# Revit family: 07. Wichmann Kabelbox W120
name_source: partatom
category: HLS-Bauteile
revit_build: Autodesk Revit 2018 (Build: 20170223_1515(x64)
units: mm (PartAtom-declared; Revit-internal decimal feet)

## family parameters
Basisbauteil = Wand
Beim Laden mit Abzugskörper schneiden = Nein
Bemaßung runder Anschluss = Durchmesser verwenden
Gemeinsam genutzt = Nein
Immer vertikal = Ja
Raumberechnungspunkt = Nein
Teiletyp = Normal

## types (68) — shared parameters
Rohbauöffnung = Ja
Tbox = 350 mm  [stored 1.14829 ft]

## per-type parameters (varying)
| type | BA | BI | BR | HA | HAN | HI | HR |
| Kabelbox W120, 90x200x350 mm | 640 mm | 610 mm | 680 mm | 100 mm  [stored 0.328084 ft] | W120090200 | 64 mm | 140 mm |
| Kabelbox W120, 90x180x350 mm | 180 mm | 150 mm  [stored 0.492126 ft] | 220 mm | 90 mm | W120090180 | 56 mm | 130 mm |
| Kabelbox W120, 90x160x350 mm | 160 mm | 130 mm | 200 mm  [stored 0.656168 ft] | 90 mm | W120090160 | 56 mm | 130 mm |
| Kabelbox W120, 90x120x350 mm | 120 mm  [stored 0.393701 ft] | 90 mm | 160 mm | 90 mm | W120090120 | 56 mm | 130 mm |
| Kabelbox W120, 90x90x350 mm | 90 mm | 60 mm | 130 mm | 90 mm | W120090090 | 56 mm | 130 mm |
| Kabelbox W120, 80x580x350 mm | 580 mm | 550 mm | 620 mm | 80 mm  [stored 0.262467 ft] | 00090090 | 50 mm  [stored 0.164042 ft] | 120 mm  [stored 0.393701 ft] |
| Kabelbox W120, 80x535x350 mm | 535 mm | 505 mm | 575 mm | 80 mm  [stored 0.262467 ft] | W120080535 | 50 mm  [stored 0.164042 ft] | 120 mm  [stored 0.393701 ft] |
| Kabelbox W120, 80x480x350 mm | 480 mm | 450 mm | 520 mm | 80 mm  [stored 0.262467 ft] | W120080480 | 50 mm  [stored 0.164042 ft] | 120 mm  [stored 0.393701 ft] |
| Kabelbox W120, 80x435x350 mm | 435 mm | 405 mm | 475 mm | 80 mm  [stored 0.262467 ft] | W120080435 | 50 mm  [stored 0.164042 ft] | 120 mm  [stored 0.393701 ft] |
| Kabelbox W120, 80x380x350 mm | 380 mm | 350 mm  [stored 1.14829 ft] | 420 mm | 80 mm  [stored 0.262467 ft] | W120080380 | 50 mm  [stored 0.164042 ft] | 120 mm  [stored 0.393701 ft] |
| Kabelbox W120, 80x335x350 mm | 335 mm | 305 mm | 375 mm | 80 mm  [stored 0.262467 ft] | W120080335 | 50 mm  [stored 0.164042 ft] | 120 mm  [stored 0.393701 ft] |
| Kabelbox W120, 80x280x350 mm | 280 mm  [stored 0.918635 ft] | 250 mm | 320 mm  [stored 1.04987 ft] | 80 mm  [stored 0.262467 ft] | W120080280 | 50 mm  [stored 0.164042 ft] | 120 mm  [stored 0.393701 ft] |
| Kabelbox W120, 80x240x350 mm | 240 mm | 210 mm | 280 mm  [stored 0.918635 ft] | 80 mm  [stored 0.262467 ft] | W120080240 | 50 mm  [stored 0.164042 ft] | 120 mm  [stored 0.393701 ft] |
| Kabelbox W120, 80x200x350 mm | 200 mm  [stored 0.656168 ft] | 170 mm | 240 mm | 80 mm  [stored 0.262467 ft] | W120080200 | 50 mm  [stored 0.164042 ft] | 120 mm  [stored 0.393701 ft] |
| Kabelbox W120, 80x180x350 mm | 180 mm | 150 mm  [stored 0.492126 ft] | 220 mm | 80 mm  [stored 0.262467 ft] | W120080180 | 50 mm  [stored 0.164042 ft] | 120 mm  [stored 0.393701 ft] |
| Kabelbox W120, 80x160x350 mm | 160 mm | 130 mm | 200 mm  [stored 0.656168 ft] | 80 mm  [stored 0.262467 ft] | W120080160 | 50 mm  [stored 0.164042 ft] | 120 mm  [stored 0.393701 ft] |
| Kabelbox W120, 80x120x350 mm | 120 mm  [stored 0.393701 ft] | 90 mm | 160 mm | 80 mm  [stored 0.262467 ft] | W120080120 | 50 mm  [stored 0.164042 ft] | 120 mm  [stored 0.393701 ft] |
| Kabelbox W120, 90x535x350 mm | 535 mm | 505 mm | 575 mm | 90 mm | W120090535 | 56 mm | 130 mm |
| Kabelbox W120, 90x480x350 mm | 480 mm | 450 mm | 520 mm | 90 mm | W120090480 | 56 mm | 130 mm |
| Kabelbox W120, 90x435x350 mm | 435 mm | 405 mm | 475 mm | 90 mm | W120090435 | 56 mm | 130 mm |
| Kabelbox W120, 90x380x350 mm | 380 mm | 350 mm  [stored 1.14829 ft] | 420 mm | 90 mm | W120090380 | 56 mm | 130 mm |
| Kabelbox W120, 90x335x350 mm | 335 mm | 305 mm | 375 mm | 90 mm | W120090335 | 56 mm | 130 mm |
| Kabelbox W120, 90x280x350 mm | 280 mm  [stored 0.918635 ft] | 250 mm | 320 mm  [stored 1.04987 ft] | 90 mm | W120090280 | 56 mm | 130 mm |
| Kabelbox W120, 90x240x350 mm | 240 mm | 210 mm | 280 mm  [stored 0.918635 ft] | 90 mm | W120090240 | 56 mm | 130 mm |
| Kabelbox W120, 80x640x350 mm | 640 mm | 610 mm | 680 mm | 80 mm  [stored 0.262467 ft] | W120080640 | 50 mm  [stored 0.164042 ft] | 120 mm  [stored 0.393701 ft] |
| Kabelbox W120, 60x580x350 mm | 580 mm | 550 mm | 620 mm | 60 mm | W120060580 | 33 mm | 100 mm  [stored 0.328084 ft] |
| Kabelbox W120, 60x640x350 mm | 640 mm | 610 mm | 680 mm | 60 mm | W120060640 | 33 mm | 100 mm  [stored 0.328084 ft] |
| Kabelbox W120, 80x90x350 mm | 90 mm | 60 mm | 130 mm | 80 mm  [stored 0.262467 ft] | W120080090 | 50 mm  [stored 0.164042 ft] | 120 mm  [stored 0.393701 ft] |
| Kabelbox W120, 90x580x350 mm | 580 mm | 550 mm | 620 mm | 90 mm | W120090580 | 56 mm | 130 mm |
| Kabelbox W120, 100x120x350 mm | 120 mm  [stored 0.393701 ft] | 90 mm | 160 mm | 100 mm  [stored 0.328084 ft] | W120100120 | 64 mm | 140 mm |
| Kabelbox W120, 100x160x350 mm | 160 mm | 130 mm | 200 mm  [stored 0.656168 ft] | 100 mm  [stored 0.328084 ft] | W120100160 | 64 mm | 140 mm |
| Kabelbox W120, 100x180x350 mm | 180 mm | 150 mm  [stored 0.492126 ft] | 220 mm | 100 mm  [stored 0.328084 ft] | W120100180 | 64 mm | 140 mm |
| Kabelbox W120, 100x380x350 mm | 380 mm | 350 mm  [stored 1.14829 ft] | 420 mm | 100 mm  [stored 0.328084 ft] | W120100380 | 64 mm | 140 mm |
| Kabelbox W120, 90x640x350 mm | 640 mm | 610 mm | 680 mm | 90 mm | W120090640 | 56 mm | 130 mm |
| Kabelbox W120, 100x240x350 mm | 240 mm | 210 mm | 280 mm  [stored 0.918635 ft] | 100 mm  [stored 0.328084 ft] | W120100240 | 64 mm | 140 mm |
| Kabelbox W120, 100x200x350 mm | 200 mm  [stored 0.656168 ft] | 170 mm | 240 mm | 100 mm  [stored 0.328084 ft] | W120100200 | 64 mm | 140 mm |
| Kabelbox W120, 100x435x350 mm | 435 mm | 405 mm | 475 mm | 100 mm  [stored 0.328084 ft] | W120100435 | 64 mm | 140 mm |
| Kabelbox W120, 100x335x350 mm | 335 mm | 305 mm | 375 mm | 100 mm  [stored 0.328084 ft] | W120100335
W120100335
W120100335 | 64 mm | 140 mm |
| Kabelbox W120, 100x280x350 mm | 280 mm  [stored 0.918635 ft] | 250 mm | 320 mm  [stored 1.04987 ft] | 100 mm  [stored 0.328084 ft] | W120100280 | 64 mm | 140 mm |
| Kabelbox W120, 100x580x350 mm | 580 mm | 550 mm | 620 mm | 100 mm  [stored 0.328084 ft] | W120100580 | 64 mm | 140 mm |
| Kabelbox W120, 100x640x350 mm | 640 mm | 610 mm | 680 mm | 100 mm  [stored 0.328084 ft] | W120100640 | 64 mm | 140 mm |
| Kabelbox W120, 110x120x350 mm | 120 mm  [stored 0.393701 ft] | 90 mm | 160 mm | 110 mm | W120110120 | 70 mm | 150 mm  [stored 0.492126 ft] |
| Kabelbox W120, 100x480x350 mm | 480 mm | 450 mm | 520 mm | 100 mm  [stored 0.328084 ft] | W120100480 | 64 mm | 140 mm |
| Kabelbox W120, 100x535x350 mm | 535 mm | 505 mm | 575 mm | 100 mm  [stored 0.328084 ft] | W120100535 | 64 mm | 140 mm |
| Kabelbox W120, 110x180x350 mm | 180 mm | 150 mm  [stored 0.492126 ft] | 220 mm | 110 mm | W120110180 | 70 mm | 150 mm  [stored 0.492126 ft] |
| Kabelbox W120, 110x160x350 mm | 160 mm | 130 mm | 200 mm  [stored 0.656168 ft] | 110 mm | W120110160 | 70 mm | 150 mm  [stored 0.492126 ft] |
| Kabelbox W120, 110x280x350 mm | 280 mm  [stored 0.918635 ft] | 250 mm | 320 mm  [stored 1.04987 ft] | 110 mm | W120110280 | 70 mm | 150 mm  [stored 0.492126 ft] |
| Kabelbox W120, 110x240x350 mm | 240 mm | 210 mm | 280 mm  [stored 0.918635 ft] | 110 mm | W120110240 | 70 mm | 150 mm  [stored 0.492126 ft] |
| Kabelbox W120, 110x200x350 mm | 200 mm  [stored 0.656168 ft] | 170 mm | 240 mm | 110 mm | W120110200 | 70 mm | 150 mm  [stored 0.492126 ft] |
| Kabelbox W120, 110x435x350 mm | 435 mm | 405 mm | 475 mm | 110 mm | W120110435 | 70 mm | 150 mm  [stored 0.492126 ft] |
| Kabelbox W120, 110x480x350 mm | 480 mm | 450 mm | 520 mm | 110 mm | W120110480 | 70 mm | 150 mm  [stored 0.492126 ft] |
| Kabelbox W120, 110x535x350 mm | 535 mm | 505 mm | 575 mm | 110 mm | W120110535 | 70 mm | 150 mm  [stored 0.492126 ft] |
| Kabelbox W120, 110x335x350 mm | 335 mm | 305 mm | 375 mm | 110 mm | W120110535 | 70 mm | 150 mm  [stored 0.492126 ft] |
| Kabelbox W120, 110x380x350 mm | 380 mm | 350 mm  [stored 1.14829 ft] | 420 mm | 110 mm | W120110380 | 70 mm | 150 mm  [stored 0.492126 ft] |
| Kabelbox W120, 110x640x350 mm | 640 mm | 610 mm | 680 mm | 110 mm | W120110640 | 70 mm | 150 mm  [stored 0.492126 ft] |
| Kabelbox W120, 110x580x350 mm | 580 mm | 550 mm | 620 mm | 110 mm | W120110580 | 70 mm | 150 mm  [stored 0.492126 ft] |
| Kabelbox W120, 60x160x350 mm | 160 mm | 130 mm | 200 mm  [stored 0.656168 ft] | 60 mm | W120060160 | 33 mm | 100 mm  [stored 0.328084 ft] |
| Kabelbox W120, 60x120x350 mm | 120 mm  [stored 0.393701 ft] | 90 mm | 160 mm | 60 mm | W120060120 | 33 mm | 100 mm  [stored 0.328084 ft] |
| Kabelbox W120, 60x90x350 mm | 90 mm | 60 mm | 130 mm | 60 mm | W120060090 | 33 mm | 100 mm  [stored 0.328084 ft] |
| Kabelbox W120, 60x240x350 mm | 240 mm | 210 mm | 280 mm  [stored 0.918635 ft] | 60 mm | W120060240 | 33 mm | 100 mm  [stored 0.328084 ft] |
| Kabelbox W120, 60x280x350 mm | 280 mm  [stored 0.918635 ft] | 250 mm | 320 mm  [stored 1.04987 ft] | 60 mm | W120060280 | 33 mm | 100 mm  [stored 0.328084 ft] |
| Kabelbox W120, 60x335x350 mm | 335 mm | 305 mm | 375 mm | 60 mm | W120060335 | 33 mm | 100 mm  [stored 0.328084 ft] |
| Kabelbox W120, 60x180x350 mm | 180 mm | 150 mm  [stored 0.492126 ft] | 220 mm | 60 mm | W120060180 | 33 mm | 100 mm  [stored 0.328084 ft] |
| Kabelbox W120, 60x200x350 mm | 200 mm  [stored 0.656168 ft] | 170 mm | 240 mm | 60 mm | W120060200 | 33 mm | 100 mm  [stored 0.328084 ft] |
| Kabelbox W120, 60x435x350 mm | 435 mm | 405 mm | 475 mm | 60 mm | W120060435 | 33 mm | 100 mm  [stored 0.328084 ft] |
| Kabelbox W120, 60x380x350 mm | 380 mm | 350 mm  [stored 1.14829 ft] | 420 mm | 60 mm | W120060380 | 33 mm | 100 mm  [stored 0.328084 ft] |
| Kabelbox W120, 60x535x350 mm | 535 mm | 505 mm | 575 mm | 60 mm | W120060535 | 33 mm | 100 mm  [stored 0.328084 ft] |
| Kabelbox W120, 60x480x350 mm | 480 mm | 450 mm | 520 mm | 60 mm | W120060480 | 33 mm | 100 mm  [stored 0.328084 ft] |

note: [stored X ft] marks values corroborated as IEEE doubles in the binary element streams (Revit-internal decimal feet)
